# Revit family: WT-Structural Tee
name_source: partatom
category: Structural Framing
revit_build: Autodesk Revit Architecture 2012 (Build: 20110210_1515)
units: mm (PartAtom-declared; Revit-internal decimal feet)

## types (275) — shared parameters
Assembly Code = B10

## per-type parameters (varying)
| type | A | W | bf | d | k | kr | tf | tw |
| WT22X167.5 | 49.2 in² | 168 | 1' - 3 7/8" | 1' - 10" | 0' - 2 5/8" | 0' - 0 7/8" | 0' - 1 3/4" | 0' - 1" |
| WT22X145 | 42.7 in² | 145 | 1' - 3 13/16" | 1' - 9 13/16" | 0' - 2 7/16" | 0' - 0 7/8" | 0' - 1 9/16" | 0' - 0 7/8" |
| WT22X131 | 38.4 in² | 131 | 1' - 3 13/16" | 1' - 9 11/16" | 0' - 2 1/4" | 0' - 0 13/16" | 0' - 1 7/16" | 0' - 0 13/16" |
| WT22X115 | 33.8 in² | 115 | 1' - 3 13/16" | 1' - 9 1/2" | 0' - 2 1/16" | 0' - 0 13/16" | 0' - 1 1/4" | 0' - 0 11/16" |
| WT20X296.5 | 87.2 in² | 296 | 1' - 4 11/16" | 1' - 9 1/2" | 0' - 4 1/2" | 0' - 1 1/4" | 0' - 3 1/4" | 0' - 1 13/16" |
| WT20X251.5 | 73.9 in² | 252 | 1' - 4 3/8" | 1' - 9" | 0' - 4" | 0' - 1 1/4" | 0' - 2 3/4" | 0' - 1 9/16" |
| WT20X215.5 | 63.4 in² | 215 | 1' - 4 3/16" | 1' - 8 5/8" | 0' - 3 5/8" | 0' - 1 1/4" | 0' - 2 3/8" | 0' - 1 5/16" |
| WT20X198.5 | 58.4 in² | 198 | 1' - 4 1/8" | 1' - 8 1/2" | 0' - 3 1/2" | 0' - 1 5/16" | 0' - 2 3/16" | 0' - 1 1/4" |
| WT20X186 | 54.6 in² | 186 | 1' - 4 1/8" | 1' - 8 5/16" | 0' - 3 5/16" | 0' - 1 1/4" | 0' - 2 1/16" | 0' - 1 3/16" |
| WT20X181 | 53.3 in² | 181 | 1' - 4" | 1' - 8 5/16" | 0' - 3 1/4" | 0' - 1 1/4" | 0' - 2" | 0' - 1 1/8" |
| WT20X162 | 47.7 in² | 162 | 1' - 3 7/8" | 1' - 8 1/8" | 0' - 3 1/16" | 0' - 1 1/4" | 0' - 1 13/16" | 0' - 1" |
| WT20X148.5 | 43.7 in² | 148 | 1' - 3 13/16" | 1' - 7 7/8" | 0' - 2 15/16" | 0' - 1 5/16" | 0' - 1 5/8" | 0' - 0 15/16" |
| WT20X138.5 | 40.7 in² | 138 | 1' - 3 13/16" | 1' - 7 13/16" | 0' - 2 7/8" | 0' - 1 5/16" | 0' - 1 9/16" | 0' - 0 13/16" |
| WT20X124.5 | 36.7 in² | 125 | 1' - 3 13/16" | 1' - 7 11/16" | 0' - 2 11/16" | 0' - 1 1/4" | 0' - 1 7/16" | 0' - 0 3/4" |
| WT20X107.5 | 31.7 in² | 108 | 1' - 3 13/16" | 1' - 7 1/2" | 0' - 2 1/2" | 0' - 1 1/4" | 0' - 1 1/4" | 0' - 0 5/8" |
| WT20X99.5 | 29.2 in² | 100 | 1' - 3 13/16" | 1' - 7 5/16" | 0' - 2 5/16" | 0' - 1 1/4" | 0' - 1 1/16" | 0' - 0 5/8" |
| WT20X196 | 57.6 in² | 196 | 1' - 0 3/8" | 1' - 8 13/16" | 0' - 3 13/16" | 0' - 1 5/16" | 0' - 2 1/2" | 0' - 1 7/16" |
| WT20X165.5 | 48.7 in² | 166 | 1' - 0 3/16" | 1' - 8 3/8" | 0' - 3 3/8" | 0' - 1 1/4" | 0' - 2 1/8" | 0' - 1 1/4" |
| WT20X163.5 | 48 in² | 164 | 1' - 0 1/8" | 1' - 8 3/8" | 0' - 3 3/8" | 0' - 1 1/4" | 0' - 2 1/8" | 0' - 1 3/16" |
| WT20X147 | 43.1 in² | 147 | 1' - 0" | 1' - 8 3/16" | 0' - 3 3/16" | 0' - 1 1/4" | 0' - 1 15/16" | 0' - 1 1/16" |
| WT20X139 | 41 in² | 139 | 1' - 0" | 1' - 8 1/8" | 0' - 3 1/16" | 0' - 1 1/4" | 0' - 1 13/16" | 0' - 1" |
| WT20X132 | 38.8 in² | 132 | 0' - 11 7/8" | 1' - 8" | 0' - 3" | 0' - 1 1/4" | 0' - 1 3/4" | 0' - 0 15/16" |
| WT20X117.5 | 34.5 in² | 118 | 0' - 11 7/8" | 1' - 7 13/16" | 0' - 2 7/8" | 0' - 1 5/16" | 0' - 1 9/16" | 0' - 0 13/16" |
| WT20X105.5 | 31 in² | 106 | 0' - 11 13/16" | 1' - 7 11/16" | 0' - 2 11/16" | 0' - 1 1/4" | 0' - 1 7/16" | 0' - 0 3/4" |
| WT20X91.5 | 26.7 in² | 91.5 | 0' - 11 13/16" | 1' - 7 1/2" | 0' - 2 1/2" | 0' - 1 5/16" | 0' - 1 3/16" | 0' - 0 5/8" |
| WT20X83.5 | 24.6 in² | 83.5 | 0' - 11 13/16" | 1' - 7 5/16" | 0' - 2 5/16" | 0' - 1 5/16" | 0' - 1" | 0' - 0 5/8" |
| WT20X74.5 | 21.9 in² | 74.5 | 0' - 11 13/16" | 1' - 7 1/8" | 0' - 2 1/8" | 0' - 1 5/16" | 0' - 0 13/16" | 0' - 0 5/8" |
| WT18X400 | 118 in² | 400 | 1' - 6" | 1' - 9" | 0' - 5 9/16" | 0' - 1 1/4" | 0' - 4 5/16" | 0' - 2 3/8" |
| WT18X326 | 96.1 in² | 325 | 1' - 5 5/8" | 1' - 8 3/16" | 0' - 4 13/16" | 0' - 1 1/4" | 0' - 3 9/16" | 0' - 2" |
| WT18X264.5 | 77.8 in² | 264 | 1' - 5 3/16" | 1' - 7 5/8" | 0' - 4 3/16" | 0' - 1 1/4" | 0' - 2 15/16" | 0' - 1 5/8" |
| WT18X243.5 | 71.7 in² | 244 | 1' - 5 1/8" | 1' - 7 11/16" | 0' - 4" | 0' - 1 5/16" | 0' - 2 11/16" | 0' - 1 1/2" |
| WT18X220.5 | 64.9 in² | 220 | 1' - 5" | 1' - 7 1/8" | 0' - 3 11/16" | 0' - 1 1/4" | 0' - 2 7/16" | 0' - 1 3/8" |
| WT18X197.5 | 58.2 in² | 198 | 1' - 4 13/16" | 1' - 6 7/8" | 0' - 3 7/16" | 0' - 1 1/4" | 0' - 2 3/16" | 0' - 1 1/4" |
| WT18X180.5 | 53 in² | 180 | 1' - 4 11/16" | 1' - 6 11/16" | 0' - 3 1/4" | 0' - 1 1/4" | 0' - 2" | 0' - 1 1/8" |
| WT18X165 | 48.5 in² | 165 | 1' - 4 5/8" | 1' - 6 1/2" | 0' - 3 1/8" | 0' - 1 1/4" | 0' - 1 7/8" | 0' - 1" |
| WT18X151 | 44.4 in² | 151 | 1' - 4 11/16" | 1' - 6 3/8" | 0' - 2 15/16" | 0' - 1 1/4" | 0' - 1 11/16" | 0' - 0 15/16" |
| WT18X141 | 41.5 in² | 141 | 1' - 4 5/8" | 1' - 6 5/16" | 0' - 2 13/16" | 0' - 1 1/4" | 0' - 1 9/16" | 0' - 0 7/8" |
| WT18X131 | 38.5 in² | 131 | 1' - 4 5/8" | 1' - 6 1/8" | 0' - 2 11/16" | 0' - 1 1/4" | 0' - 1 7/16" | 0' - 0 13/16" |
| WT18X123.5 | 36.3 in² | 124 | 1' - 4 1/2" | 1' - 6" | 0' - 2 5/8" | 0' - 1 1/4" | 0' - 1 3/8" | 0' - 0 13/16" |
| WT18X116 | 34.5 in² | 116 | 1' - 0 1/8" | 1' - 6 5/8" | 0' - 2 7/16" | 0' - 0 7/8" | 0' - 1 9/16" | 0' - 0 7/8" |
| WT18X128 | 37.7 in² | 128 | 1' - 0 3/16" | 1' - 6 11/16" | 0' - 2 5/8" | 0' - 0 7/8" | 0' - 1 3/4" | 0' - 0 15/16" |
| WT18X115.5 | 34.1 in² | 116 | 1' - 0 1/8" | 1' - 6 5/8" | 0' - 2 7/16" | 0' - 0 7/8" | 0' - 1 9/16" | 0' - 0 7/8" |
| WT18X105 | 30.9 in² | 105 | 1' - 0 3/16" | 1' - 6 5/16" | 0' - 2 5/16" | 0' - 0 15/16" | 0' - 1 3/8" | 0' - 0 13/16" |
| WT18X97 | 28.5 in² | 97 | 1' - 0 1/8" | 1' - 6 3/16" | 0' - 2 3/16" | 0' - 0 15/16" | 0' - 1 1/4" | 0' - 0 3/4" |
| WT18X91 | 26.8 in² | 91 | 1' - 0 1/8" | 1' - 6 3/16" | 0' - 2 1/8" | 0' - 0 15/16" | 0' - 1 3/16" | 0' - 0 3/4" |
| WT18X85 | 25 in² | 85 | 1' - 0" | 1' - 6 1/8" | 0' - 2" | 0' - 0 7/8" | 0' - 1 1/8" | 0' - 0 11/16" |
| WT18X80 | 23.5 in² | 80 | 1' - 0" | 1' - 6" | 0' - 1 15/16" | 0' - 0 15/16" | 0' - 1" | 0' - 0 5/8" |
| WT18X75 | 22.1 in² | 75 | 1' - 0" | 1' - 5 7/8" | 0' - 1 7/8" | 0' - 0 15/16" | 0' - 0 15/16" | 0' - 0 5/8" |
| WT18X67.5 | 19.9 in² | 67.5 | 1' - 0" | 1' - 5 13/16" | 0' - 1 11/16" | 0' - 0 7/8" | 0' - 0 13/16" | 0' - 0 5/8" |
| WT16.5X193.5 | 57 in² | 194 | 1' - 4 3/16" | 1' - 6" | 0' - 3 3/16" | 0' - 0 15/16" | 0' - 2 1/4" | 0' - 1 1/4" |
| WT16.5X177 | 52.1 in² | 177 | 1' - 4 1/8" | 1' - 5 13/16" | 0' - 2 15/16" | 0' - 0 7/8" | 0' - 2 1/16" | 0' - 1 3/16" |
| WT16.5X159 | 46.8 in² | 159 | 1' - 4" | 1' - 5 5/8" | 0' - 2 3/4" | 0' - 0 7/8" | 0' - 1 7/8" | 0' - 1 1/16" |
| WT16.5X145.5 | 42.8 in² | 146 | 1' - 3 7/8" | 1' - 5 3/8" | 0' - 2 5/8" | 0' - 0 7/8" | 0' - 1 3/4" | 0' - 0 15/16" |
| WT16.5X131.5 | 38.7 in² | 132 | 1' - 3 13/16" | 1' - 5 5/16" | 0' - 2 7/16" | 0' - 0 7/8" | 0' - 1 9/16" | 0' - 0 7/8" |
| WT16.5X120.5 | 35.5 in² | 120 | 1' - 3 7/8" | 1' - 5 1/8" | 0' - 2 1/4" | 0' - 0 7/8" | 0' - 1 3/8" | 0' - 0 13/16" |
| WT16.5X110.5 | 32.6 in² | 110 | 1' - 3 13/16" | 1' - 5" | 0' - 2 1/8" | 0' - 0 7/8" | 0' - 1 1/4" | 0' - 0 3/4" |
| WT16.5X100.5 | 29.6 in² | 100 | 1' - 3 11/16" | 1' - 4 13/16" | 0' - 2" | 0' - 0 7/8" | 0' - 1 1/8" | 0' - 0 11/16" |
| WT16.5X84.5 | 24.8 in² | 84.5 | 0' - 11 1/2" | 1' - 4 7/8" | 0' - 2 1/8" | 0' - 0 7/8" | 0' - 1 1/4" | 0' - 0 11/16" |
| WT16.5X76 | 22.4 in² | 76 | 0' - 11 5/8" | 1' - 4 11/16" | 0' - 1 15/16" | 0' - 0 7/8" | 0' - 1 1/16" | 0' - 0 5/8" |
| WT16.5X70.5 | 20.8 in² | 70.5 | 0' - 11 1/2" | 1' - 4 11/16" | 0' - 1 13/16" | 0' - 0 7/8" | 0' - 0 15/16" | 0' - 0 5/8" |
| WT16.5X65 | 19.2 in² | 65 | 0' - 11 1/2" | 1' - 4 1/2" | 0' - 1 3/4" | 0' - 0 7/8" | 0' - 0 7/8" | 0' - 0 9/16" |
| WT16.5X59 | 17.3 in² | 59 | 0' - 11 1/2" | 1' - 4 3/8" | 0' - 1 5/8" | 0' - 0 7/8" | 0' - 0 3/4" | 0' - 0 9/16" |
| WT15X195.5 | 57.6 in² | 196 | 1' - 3 5/8" | 1' - 4 5/8" | 0' - 3 3/8" | 0' - 0 15/16" | 0' - 2 7/16" | 0' - 1 3/8" |
| WT15X178.5 | 52.5 in² | 178 | 1' - 3 1/2" | 1' - 4 3/8" | 0' - 3 1/8" | 0' - 0 7/8" | 0' - 2 1/4" | 0' - 1 1/4" |
| WT15X163 | 47.9 in² | 163 | 1' - 3 3/8" | 1' - 4 3/16" | 0' - 2 15/16" | 0' - 0 7/8" | 0' - 2 1/16" | 0' - 1 1/8" |
| WT15X146 | 42.9 in² | 146 | 1' - 3 5/16" | 1' - 4" | 0' - 2 3/4" | 0' - 0 7/8" | 0' - 1 7/8" | 0' - 1" |
| WT15X130.5 | 38.4 in² | 130 | 1' - 3 3/16" | 1' - 3 13/16" | 0' - 2 9/16" | 0' - 0 15/16" | 0' - 1 5/8" | 0' - 0 15/16" |
| WT15X117.5 | 34.6 in² | 118 | 1' - 3 1/8" | 1' - 3 11/16" | 0' - 2 3/8" | 0' - 0 7/8" | 0' - 1 1/2" | 0' - 0 13/16" |
| WT15X105.5 | 31.1 in² | 106 | 1' - 3 1/8" | 1' - 3 1/2" | 0' - 2 1/4" | 0' - 0 15/16" | 0' - 1 5/16" | 0' - 0 3/4" |
| WT15X95.5 | 28.1 in² | 95.5 | 1' - 3" | 1' - 3 5/16" | 0' - 2 1/16" | 0' - 0 7/8" | 0' - 1 3/16" | 0' - 0 11/16" |
| WT15X86.5 | 25.5 in² | 86.5 | 1' - 3" | 1' - 3 3/16" | 0' - 2" | 0' - 0 15/16" | 0' - 1 1/16" | 0' - 0 5/8" |
| WT15X74 | 21.7 in² | 74 | 0' - 10 1/2" | 1' - 3 5/16" | 0' - 2 1/16" | 0' - 0 7/8" | 0' - 1 3/16" | 0' - 0 5/8" |
| WT15X66 | 19.4 in² | 66 | 0' - 10 1/2" | 1' - 3 3/16" | 0' - 1 7/8" | 0' - 0 7/8" | 0' - 1" | 0' - 0 5/8" |
| WT15X62 | 18.2 in² | 62 | 0' - 10 1/2" | 1' - 3 1/8" | 0' - 1 13/16" | 0' - 0 7/8" | 0' - 0 15/16" | 0' - 0 9/16" |
| WT15X58 | 17.1 in² | 58 | 0' - 10 1/2" | 1' - 3" | 0' - 1 3/4" | 0' - 0 7/8" | 0' - 0 7/8" | 0' - 0 9/16" |
| WT15X54 | 15.9 in² | 54 | 0' - 10 1/2" | 1' - 2 7/8" | 0' - 1 11/16" | 0' - 0 15/16" | 0' - 0 3/4" | 0' - 0 9/16" |
| WT15X49.5 | 14.5 in² | 49.5 | 0' - 10 1/2" | 1' - 2 13/16" | 0' - 1 9/16" | 0' - 0 7/8" | 0' - 0 11/16" | 0' - 0 1/2" |
| WT15X45 | 13.2 in² | 45 | 0' - 10 3/8" | 1' - 2 13/16" | 0' - 1 1/2" | 0' - 0 7/8" | 0' - 0 5/8" | 0' - 0 1/2" |
| WT13.5X269.5 | 79.3 in² | 270 | 1' - 3 5/16" | 1' - 4 5/16" | 0' - 4 7/16" | 0' - 0 7/8" | 0' - 3 9/16" | 0' - 2" |
| WT13.5X184 | 54.2 in² | 184 | 1' - 2 11/16" | 1' - 3 3/16" | 0' - 3 3/8" | 0' - 0 7/8" | 0' - 2 1/2" | 0' - 1 3/8" |
| WT13.5X168 | 49.5 in² | 168 | 1' - 2 5/8" | 1' - 3" | 0' - 3 3/16" | 0' - 0 15/16" | 0' - 2 1/4" | 0' - 1 1/4" |
| WT13.5X153.5 | 45.2 in² | 154 | 1' - 2 3/8" | 1' - 2 13/16" | 0' - 3" | 0' - 0 15/16" | 0' - 2 1/16" | 0' - 1 3/16" |
| WT13.5X140.5 | 41.4 in² | 140 | 1' - 2 3/8" | 1' - 2 5/8" | 0' - 2 13/16" | 0' - 0 7/8" | 0' - 1 15/16" | 0' - 1 1/16" |
| WT13.5X129 | 38 in² | 129 | 1' - 2 5/16" | 1' - 2 1/2" | 0' - 2 11/16" | 0' - 0 15/16" | 0' - 1 3/4" | 0' - 1" |
| WT13.5X117.5 | 34.7 in² | 118 | 1' - 2 3/16" | 1' - 2 5/16" | 0' - 2 1/2" | 0' - 0 7/8" | 0' - 1 5/8" | 0' - 0 15/16" |
| WT13.5X108.5 | 32 in² | 108 | 1' - 2 1/8" | 1' - 2 3/16" | 0' - 2 3/8" | 0' - 0 7/8" | 0' - 1 1/2" | 0' - 0 13/16" |
| WT13.5X97 | 28.6 in² | 97 | 1' - 2" | 1' - 2 1/8" | 0' - 2 1/4" | 0' - 0 15/16" | 0' - 1 5/16" | 0' - 0 3/4" |
| WT13.5X89 | 26.2 in² | 89 | 1' - 2 1/8" | 1' - 1 7/8" | 0' - 2 1/16" | 0' - 0 7/8" | 0' - 1 3/16" | 0' - 0 3/4" |
| WT13.5X80.5 | 23.8 in² | 80.5 | 1' - 2" | 1' - 1 13/16" | 0' - 2" | 0' - 0 15/16" | 0' - 1 1/16" | 0' - 0 11/16" |
| WT13.5X73 | 21.6 in² | 73 | 1' - 2" | 1' - 1 11/16" | 0' - 1 7/8" | 0' - 0 7/8" | 0' - 1" | 0' - 0 5/8" |
| WT13.5X64.5 | 18.9 in² | 64.5 | 0' - 10" | 1' - 1 13/16" | 0' - 2" | 0' - 0 7/8" | 0' - 1 1/8" | 0' - 0 5/8" |
| WT13.5X57 | 16.8 in² | 57 | 0' - 10 1/8" | 1' - 1 5/8" | 0' - 1 13/16" | 0' - 0 7/8" | 0' - 0 15/16" | 0' - 0 9/16" |
| WT13.5X51 | 15 in² | 51 | 0' - 10" | 1' - 1 1/2" | 0' - 1 3/4" | 0' - 0 15/16" | 0' - 0 13/16" | 0' - 0 1/2" |
| WT13.5X47 | 13.8 in² | 47 | 0' - 10" | 1' - 1 1/2" | 0' - 1 5/8" | 0' - 0 7/8" | 0' - 0 3/4" | 0' - 0 1/2" |
| WT13.5X42 | 12.4 in² | 42 | 0' - 10" | 1' - 1 3/8" | 0' - 1 9/16" | 0' - 0 15/16" | 0' - 0 5/8" | 0' - 0 7/16" |
| WT12X185 | 54.4 in² | 185 | 1' - 1 11/16" | 1' - 2" | 0' - 3 5/8" | 0' - 0 7/8" | 0' - 2 3/4" | 0' - 1 1/2" |
| WT12X167.5 | 49.2 in² | 168 | 1' - 1 1/2" | 1' - 1 13/16" | 0' - 3 3/8" | 0' - 0 7/8" | 0' - 2 1/2" | 0' - 1 3/8" |
| WT12X153 | 44.9 in² | 153 | 1' - 1 3/8" | 1' - 1 5/8" | 0' - 3 3/16" | 0' - 0 15/16" | 0' - 2 1/4" | 0' - 1 1/4" |
| WT12X139.5 | 41 in² | 140 | 1' - 1 5/16" | 1' - 1 3/8" | 0' - 3" | 0' - 0 15/16" | 0' - 2 1/16" | 0' - 1 3/16" |
| WT12X125 | 36.8 in² | 125 | 1' - 1 3/16" | 1' - 1 3/16" | 0' - 2 13/16" | 0' - 0 15/16" | 0' - 1 7/8" | 0' - 1 1/16" |
| WT12X114.5 | 33.6 in² | 114 | 1' - 1 1/8" | 1' - 1" | 0' - 2 5/8" | 0' - 0 7/8" | 0' - 1 3/4" | 0' - 0 15/16" |
| WT12X103.5 | 30.4 in² | 103 | 1' - 1" | 1' - 0 7/8" | 0' - 2 1/2" | 0' - 0 15/16" | 0' - 1 9/16" | 0' - 0 7/8" |
| WT12X96 | 28.1 in² | 96 | 1' - 1" | 1' - 0 11/16" | 0' - 2 3/8" | 0' - 0 15/16" | 0' - 1 7/16" | 0' - 0 13/16" |
| WT12X88 | 25.8 in² | 88 | 1' - 0 7/8" | 1' - 0 5/8" | 0' - 2 1/4" | 0' - 0 15/16" | 0' - 1 5/16" | 0' - 0 3/4" |
| WT12X81 | 23.9 in² | 81 | 1' - 1" | 1' - 0 1/2" | 0' - 2 1/8" | 0' - 0 7/8" | 0' - 1 1/4" | 0' - 0 11/16" |
| WT12X73 | 21.5 in² | 73 | 1' - 0 7/8" | 1' - 0 3/8" | 0' - 2" | 0' - 0 15/16" | 0' - 1 1/16" | 0' - 0 5/8" |
| WT12X65.5 | 19.3 in² | 65.5 | 1' - 0 7/8" | 1' - 0 3/16" | 0' - 1 7/8" | 0' - 0 15/16" | 0' - 0 15/16" | 0' - 0 5/8" |
| WT12X58.5 | 17.2 in² | 58.5 | 1' - 0 13/16" | 1' - 0 1/8" | 0' - 1 3/4" | 0' - 0 7/8" | 0' - 0 7/8" | 0' - 0 9/16" |
| WT12X52 | 15.3 in² | 52 | 1' - 0 13/16" | 1' - 0" | 0' - 1 5/8" | 0' - 0 7/8" | 0' - 0 3/4" | 0' - 0 1/2" |
| WT12X51.5 | 15.1 in² | 51.5 | 0' - 9" | 1' - 0 5/16" | 0' - 1 7/8" | 0' - 0 7/8" | 0' - 1" | 0' - 0 9/16" |
| WT12X47 | 13.8 in² | 47 | 0' - 9 1/16" | 1' - 0 3/16" | 0' - 1 3/4" | 0' - 0 7/8" | 0' - 0 7/8" | 0' - 0 1/2" |
| WT12X42 | 12.4 in² | 42 | 0' - 9" | 1' - 0 1/8" | 0' - 1 11/16" | 0' - 0 15/16" | 0' - 0 3/4" | 0' - 0 1/2" |
| WT12X38 | 11.2 in² | 38 | 0' - 9" | 1' - 0" | 0' - 1 9/16" | 0' - 0 7/8" | 0' - 0 11/16" | 0' - 0 7/16" |
| WT12X34 | 10 in² | 34 | 0' - 9" | 0' - 11 7/8" | 0' - 1 1/2" | 0' - 0 15/16" | 0' - 0 9/16" | 0' - 0 7/16" |
| WT12X31 | 9.11 in² | 31 | 0' - 7 1/16" | 0' - 11 7/8" | 0' - 1 1/2" | 0' - 0 15/16" | 0' - 0 9/16" | 0' - 0 7/16" |
| WT12X27.5 | 8.1 in² | 27.5 | 0' - 7" | 0' - 11 13/16" | 0' - 1 7/16" | 0' - 0 15/16" | 0' - 0 1/2" | 0' - 0 3/8" |
| WT10.5X100.5 | 29.6 in² | 100 | 1' - 0 5/8" | 0' - 11 1/2" | 0' - 2 1/2" | 0' - 0 7/8" | 0' - 1 5/8" | 0' - 0 15/16" |
| WT10.5X91 | 26.8 in² | 91 | 1' - 0 1/2" | 0' - 11 3/8" | 0' - 2 3/8" | 0' - 0 7/8" | 0' - 1 1/2" | 0' - 0 13/16" |
| WT10.5X83 | 24.4 in² | 83 | 1' - 0 3/8" | 0' - 11 3/16" | 0' - 2 1/4" | 0' - 0 7/8" | 0' - 1 3/8" | 0' - 0 3/4" |
| WT10.5X73.5 | 21.6 in² | 73.5 | 1' - 0 1/2" | 0' - 11" | 0' - 2" | 0' - 0 7/8" | 0' - 1 1/8" | 0' - 0 3/4" |
| WT10.5X66 | 19.4 in² | 66 | 1' - 0 3/8" | 0' - 10 7/8" | 0' - 1 15/16" | 0' - 0 7/8" | 0' - 1 1/16" | 0' - 0 5/8" |
| WT10.5X61 | 17.9 in² | 61 | 1' - 0 3/8" | 0' - 10 13/16" | 0' - 1 13/16" | 0' - 0 7/8" | 0' - 0 15/16" | 0' - 0 5/8" |
| WT10.5X55.5 | 16.3 in² | 55.5 | 1' - 0 5/16" | 0' - 10 13/16" | 0' - 1 3/4" | 0' - 0 7/8" | 0' - 0 7/8" | 0' - 0 9/16" |
| WT10.5X50.5 | 14.9 in² | 50.5 | 1' - 0 5/16" | 0' - 10 11/16" | 0' - 1 11/16" | 0' - 0 7/8" | 0' - 0 13/16" | 0' - 0 1/2" |
| WT10.5X46.5 | 13.7 in² | 46.5 | 0' - 8 7/16" | 0' - 10 13/16" | 0' - 1 5/8" | 0' - 0 11/16" | 0' - 0 15/16" | 0' - 0 9/16" |
| WT10.5X41.5 | 12.2 in² | 41.5 | 0' - 8 3/8" | 0' - 10 11/16" | 0' - 1 1/2" | 0' - 0 11/16" | 0' - 0 13/16" | 0' - 0 1/2" |
| WT10.5X36.5 | 10.7 in² | 36.5 | 0' - 8 5/16" | 0' - 10 5/8" | 0' - 1 7/16" | 0' - 0 11/16" | 0' - 0 3/4" | 0' - 0 7/16" |
| WT10.5X34 | 10 in² | 34 | 0' - 8 1/4" | 0' - 10 5/8" | 0' - 1 3/8" | 0' - 0 11/16" | 0' - 0 11/16" | 0' - 0 7/16" |
| WT10.5X31 | 9.13 in² | 31 | 0' - 8 1/4" | 0' - 10 1/2" | 0' - 1 5/16" | 0' - 0 11/16" | 0' - 0 5/8" | 0' - 0 3/8" |
| WT10.5X27.5 | 8.1 in² | 27.5 | 0' - 8 1/4" | 0' - 10 3/8" | 0' - 1 3/16" | 0' - 0 11/16" | 0' - 0 1/2" | 0' - 0 3/8" |
| WT10.5X24 | 7.07 in² | 24 | 0' - 8 1/8" | 0' - 10 5/16" | 0' - 1 1/8" | 0' - 0 11/16" | 0' - 0 7/16" | 0' - 0 3/8" |
| WT10.5X28.5 | 8.37 in² | 28.5 | 0' - 6 9/16" | 0' - 10 1/2" | 0' - 1 5/16" | 0' - 0 11/16" | 0' - 0 5/8" | 0' - 0 3/8" |
| WT10.5X25 | 7.36 in² | 25 | 0' - 6 1/2" | 0' - 10 3/8" | 0' - 1 1/4" | 0' - 0 11/16" | 0' - 0 9/16" | 0' - 0 3/8" |
| WT10.5X22 | 6.49 in² | 22 | 0' - 6 1/2" | 0' - 10 5/16" | 0' - 1 1/8" | 0' - 0 11/16" | 0' - 0 7/16" | 0' - 0 3/8" |
| WT9X155.5 | 45.8 in² | 156 | 1' - 0" | 0' - 11 3/16" | 0' - 3 7/16" | 0' - 0 11/16" | 0' - 2 3/4" | 0' - 1 1/2" |
| WT9X141.5 | 41.6 in² | 142 | 0' - 11 7/8" | 0' - 10 7/8" | 0' - 3 3/16" | 0' - 0 11/16" | 0' - 2 1/2" | 0' - 1 3/8" |
| WT9X129 | 37.9 in² | 129 | 0' - 11 13/16" | 0' - 10 11/16" | 0' - 3" | 0' - 0 11/16" | 0' - 2 5/16" | 0' - 1 1/4" |
| WT9X117 | 34.4 in² | 117 | 0' - 11 11/16" | 0' - 10 1/2" | 0' - 2 3/4" | 0' - 0 5/8" | 0' - 2 1/8" | 0' - 1 3/16" |
| WT9X105.5 | 31.1 in² | 106 | 0' - 11 5/8" | 0' - 10 5/16" | 0' - 2 9/16" | 0' - 0 5/8" | 0' - 1 15/16" | 0' - 1 1/16" |
| WT9X96 | 28.2 in² | 97 | 0' - 11 1/2" | 0' - 10 3/16" | 0' - 2 7/16" | 0' - 0 11/16" | 0' - 1 3/4" | 0' - 0 15/16" |
| WT9X87.5 | 25.7 in² | 87.5 | 0' - 11 3/8" | 0' - 10" | 0' - 2 7/16" | 0' - 0 7/8" | 0' - 1 9/16" | 0' - 0 7/8" |
| WT9X79 | 23.2 in² | 79 | 0' - 11 5/16" | 0' - 9 7/8" | 0' - 2 3/8" | 0' - 0 15/16" | 0' - 1 7/16" | 0' - 0 13/16" |
| WT9X71.5 | 21 in² | 71.5 | 0' - 11 3/16" | 0' - 9 3/4" | 0' - 2 3/16" | 0' - 0 7/8" | 0' - 1 5/16" | 0' - 0 3/4" |
| WT9X65 | 19.1 in² | 65 | 0' - 11 3/16" | 0' - 9 5/8" | 0' - 2 1/16" | 0' - 0 7/8" | 0' - 1 3/16" | 0' - 0 11/16" |
| WT9X59.5 | 17.5 in² | 59.5 | 0' - 11 5/16" | 0' - 9 1/2" | 0' - 1 15/16" | 0' - 0 7/8" | 0' - 1 1/16" | 0' - 0 5/8" |
| WT9X53 | 15.6 in² | 53 | 0' - 11 3/16" | 0' - 9 3/8" | 0' - 1 13/16" | 0' - 0 7/8" | 0' - 0 15/16" | 0' - 0 9/16" |
| WT9X48.5 | 14.3 in² | 48.5 | 0' - 11 1/8" | 0' - 9 5/16" | 0' - 1 3/4" | 0' - 0 7/8" | 0' - 0 7/8" | 0' - 0 9/16" |
| WT9X43 | 12.7 in² | 43 | 0' - 11 1/8" | 0' - 9 3/16" | 0' - 1 5/8" | 0' - 0 7/8" | 0' - 0 3/4" | 0' - 0 1/2" |
| WT9X38 | 11.2 in² | 38 | 0' - 11" | 0' - 9 1/8" | 0' - 1 9/16" | 0' - 0 7/8" | 0' - 0 11/16" | 0' - 0 7/16" |
| WT9X35.5 | 10.4 in² | 35.5 | 0' - 7 5/8" | 0' - 9 1/4" | 0' - 1 1/2" | 0' - 0 11/16" | 0' - 0 13/16" | 0' - 0 1/2" |
| WT9X32.5 | 9.55 in² | 32.5 | 0' - 7 9/16" | 0' - 9 3/16" | 0' - 1 7/16" | 0' - 0 11/16" | 0' - 0 3/4" | 0' - 0 7/16" |
| WT9X30 | 8.82 in² | 30 | 0' - 7 9/16" | 0' - 9 1/8" | 0' - 1 3/8" | 0' - 0 11/16" | 0' - 0 11/16" | 0' - 0 7/16" |
| WT9X27.5 | 8.1 in² | 27.5 | 0' - 7 1/2" | 0' - 9 1/16" | 0' - 1 5/16" | 0' - 0 11/16" | 0' - 0 5/8" | 0' - 0 3/8" |
| WT9X25 | 7.33 in² | 25 | 0' - 7 1/2" | 0' - 9" | 0' - 1 1/4" | 0' - 0 11/16" | 0' - 0 9/16" | 0' - 0 3/8" |
| WT9X23 | 6.77 in² | 23 | 0' - 6 1/16" | 0' - 9" | 0' - 1 1/4" | 0' - 0 5/8" | 0' - 0 5/8" | 0' - 0 3/8" |
| WT9X20 | 5.88 in² | 20 | 0' - 6" | 0' - 8 15/16" | 0' - 1 3/16" | 0' - 0 11/16" | 0' - 0 1/2" | 0' - 0 5/16" |
| WT9X17.5 | 5.15 in² | 17.5 | 0' - 6" | 0' - 8 7/8" | 0' - 1 1/8" | 0' - 0 11/16" | 0' - 0 7/16" | 0' - 0 5/16" |
| WT8X50 | 14.7 in² | 50 | 0' - 10 3/8" | 0' - 8 1/2" | 0' - 1 7/8" | 0' - 0 7/8" | 0' - 1" | 0' - 0 9/16" |
| WT8X44.5 | 13.1 in² | 44.5 | 0' - 10 3/8" | 0' - 8 3/8" | 0' - 1 3/4" | 0' - 0 7/8" | 0' - 0 7/8" | 0' - 0 1/2" |
| WT8X38.5 | 11.3 in² | 38.5 | 0' - 10 5/16" | 0' - 8 1/4" | 0' - 1 5/8" | 0' - 0 7/8" | 0' - 0 3/4" | 0' - 0 7/16" |
| WT8X33.5 | 9.84 in² | 33.5 | 0' - 10 3/16" | 0' - 8 3/16" | 0' - 1 9/16" | 0' - 0 7/8" | 0' - 0 11/16" | 0' - 0 3/8" |
| WT8X28.5 | 8.39 in² | 28.5 | 0' - 7 1/8" | 0' - 8 1/4" | 0' - 1 3/8" | 0' - 0 11/16" | 0' - 0 11/16" | 0' - 0 7/16" |
| WT8X25 | 7.37 in² | 25 | 0' - 7 1/16" | 0' - 8 1/8" | 0' - 1 5/16" | 0' - 0 11/16" | 0' - 0 5/8" | 0' - 0 3/8" |
| WT8X22.5 | 6.63 in² | 22.5 | 0' - 7 1/16" | 0' - 8 1/16" | 0' - 1 1/4" | 0' - 0 11/16" | 0' - 0 9/16" | 0' - 0 3/8" |
| WT8X20 | 5.89 in² | 20 | 0' - 7" | 0' - 8" | 0' - 1 3/16" | 0' - 0 11/16" | 0' - 0 1/2" | 0' - 0 5/16" |
| WT8X18 | 5.29 in² | 18 | 0' - 7" | 0' - 7 15/16" | 0' - 1 1/8" | 0' - 0 11/16" | 0' - 0 7/16" | 0' - 0 5/16" |
| WT8X15.5 | 4.56 in² | 15.5 | 0' - 5 1/2" | 0' - 7 15/16" | 0' - 1 1/8" | 0' - 0 11/16" | 0' - 0 7/16" | 0' - 0 1/4" |
| WT8X13 | 3.84 in² | 13 | 0' - 5 1/2" | 0' - 7 7/8" | 0' - 1 1/16" | 0' - 0 11/16" | 0' - 0 3/8" | 0' - 0 1/4" |
| WT7X404 - Obsolete | 119 in² | 404 | 1' - 6 5/8" | 0' - 11 3/8" | 0' - 6 7/16" | 0' - 1 5/16" | 0' - 5 1/8" | 0' - 3 3/4" |
| WT7X365 | 107 in² | 365 | 1' - 5 7/8" | 0' - 11 3/16" | 0' - 6 3/16" | 0' - 1 1/4" | 0' - 4 15/16" | 0' - 3 1/16" |
| WT7X332.5 | 97.8 in² | 332 | 1' - 5 11/16" | 0' - 10 13/16" | 0' - 5 13/16" | 0' - 1 5/16" | 0' - 4 1/2" | 0' - 2 13/16" |
| WT7X302.5 | 88.9 in² | 302 | 1' - 5 3/8" | 0' - 10 1/2" | 0' - 5 7/16" | 0' - 1 1/4" | 0' - 4 3/16" | 0' - 2 5/8" |
| WT7X275 | 80.9 in² | 275 | 1' - 5 3/16" | 0' - 10 1/8" | 0' - 5 1/8" | 0' - 1 5/16" | 0' - 3 13/16" | 0' - 2 3/8" |
| WT7X250 | 73.5 in² | 250 | 1' - 5" | 0' - 9 13/16" | 0' - 4 13/16" | 0' - 1 5/16" | 0' - 3 1/2" | 0' - 2 3/16" |
| WT7X227.5 | 66.9 in² | 228 | 1' - 4 13/16" | 0' - 9 1/2" | 0' - 4 1/2" | 0' - 1 5/16" | 0' - 3 3/16" | 0' - 2" |
| WT7X213 | 62.6 in² | 213 | 1' - 4 11/16" | 0' - 9 5/16" | 0' - 4 5/16" | 0' - 1 1/4" | 0' - 3 1/16" | 0' - 1 7/8" |
| WT7X199 | 58.5 in² | 199 | 1' - 4 5/8" | 0' - 9 1/8" | 0' - 4 1/8" | 0' - 1 1/4" | 0' - 2 7/8" | 0' - 1 3/4" |
| WT7X185 | 54.4 in² | 185 | 1' - 4 1/2" | 0' - 8 15/16" | 0' - 3 15/16" | 0' - 1 1/4" | 0' - 2 11/16" | 0' - 1 11/16" |
| WT7X171 | 50.3 in² | 171 | 1' - 4 3/8" | 0' - 8 3/4" | 0' - 3 3/4" | 0' - 1 1/4" | 0' - 2 1/2" | 0' - 1 9/16" |
| WT7X155.5 | 45.7 in² | 156 | 1' - 4 3/16" | 0' - 8 9/16" | 0' - 3 9/16" | 0' - 1 5/16" | 0' - 2 1/4" | 0' - 1 7/16" |
| WT7X141.5 | 41.6 in² | 142 | 1' - 4 1/8" | 0' - 8 3/8" | 0' - 3 3/8" | 0' - 1 5/16" | 0' - 2 1/16" | 0' - 1 5/16" |
| WT7X128.5 | 37.8 in² | 128 | 1' - 4" | 0' - 8 3/16" | 0' - 3 3/16" | 0' - 1 5/16" | 0' - 1 7/8" | 0' - 1 3/16" |
| WT7X116.5 | 34.2 in² | 116 | 1' - 3 7/8" | 0' - 8" | 0' - 3" | 0' - 1 1/4" | 0' - 1 3/4" | 0' - 1 1/16" |
| WT7X105.5 | 31 in² | 106 | 1' - 3 13/16" | 0' - 7 7/8" | 0' - 2 7/8" | 0' - 1 5/16" | 0' - 1 9/16" | 0' - 1" |
| WT7X96.5 | 28.4 in² | 96.5 | 1' - 3 11/16" | 0' - 7 3/4" | 0' - 2 3/4" | 0' - 1 5/16" | 0' - 1 7/16" | 0' - 0 7/8" |
| WT7X88 | 25.9 in² | 88 | 1' - 3 11/16" | 0' - 7 5/8" | 0' - 2 5/8" | 0' - 1 5/16" | 0' - 1 5/16" | 0' - 0 13/16" |
| WT7X79.5 | 23.4 in² | 79.5 | 1' - 3 5/8" | 0' - 7 1/2" | 0' - 2 1/2" | 0' - 1 5/16" | 0' - 1 3/16" | 0' - 0 3/4" |
| WT7X72.5 | 21.3 in² | 72.5 | 1' - 3 1/2" | 0' - 7 3/8" | 0' - 2 3/8" | 0' - 1 5/16" | 0' - 1 1/16" | 0' - 0 11/16" |
| WT7X66 | 19.4 in² | 66 | 1' - 2 11/16" | 0' - 7 5/16" | 0' - 2 5/16" | 0' - 1 5/16" | 0' - 1" | 0' - 0 5/8" |
| WT7X60 | 17.7 in² | 60 | 1' - 2 11/16" | 0' - 7 1/4" | 0' - 2 1/4" | 0' - 1 5/16" | 0' - 0 15/16" | 0' - 0 9/16" |
| WT7X54.5 | 16 in² | 54.5 | 1' - 2 5/8" | 0' - 7 3/16" | 0' - 2 3/16" | 0' - 1 5/16" | 0' - 0 7/8" | 0' - 0 1/2" |
| WT7X49.5 | 14.6 in² | 49.5 | 1' - 2 5/8" | 0' - 7 1/16" | 0' - 2 1/16" | 0' - 1 5/16" | 0' - 0 3/4" | 0' - 0 1/2" |
| WT7X45 | 13.2 in² | 45 | 1' - 2 1/2" | 0' - 7" | 0' - 2" | 0' - 1 5/16" | 0' - 0 11/16" | 0' - 0 7/16" |
| WT7X41 | 12 in² | 41 | 0' - 10 1/8" | 0' - 7 3/16" | 0' - 1 11/16" | 0' - 0 13/16" | 0' - 0 7/8" | 0' - 0 1/2" |
| WT7X37 | 10.9 in² | 37 | 0' - 10 1/8" | 0' - 7 1/16" | 0' - 1 5/8" | 0' - 0 13/16" | 0' - 0 13/16" | 0' - 0 7/16" |
| WT7X34 | 10 in² | 34 | 0' - 10" | 0' - 7" | 0' - 1 9/16" | 0' - 0 13/16" | 0' - 0 3/4" | 0' - 0 7/16" |
| WT7X30.5 | 8.96 in² | 30.5 | 0' - 10" | 0' - 6 15/16" | 0' - 1 1/2" | 0' - 0 7/8" | 0' - 0 5/8" | 0' - 0 3/8" |
| WT7X26.5 | 7.8 in² | 26.5 | 0' - 8 1/16" | 0' - 6 15/16" | 0' - 1 1/2" | 0' - 0 13/16" | 0' - 0 11/16" | 0' - 0 3/8" |
| WT7X24 | 7.07 in² | 24 | 0' - 8" | 0' - 6 7/8" | 0' - 1 7/16" | 0' - 0 13/16" | 0' - 0 5/8" | 0' - 0 5/16" |
| WT7X21.5 | 6.31 in² | 21.5 | 0' - 8" | 0' - 6 13/16" | 0' - 1 3/8" | 0' - 0 7/8" | 0' - 0 1/2" | 0' - 0 5/16" |
| WT7X19 | 5.58 in² | 19 | 0' - 6 3/4" | 0' - 7 1/16" | 0' - 1 1/4" | 0' - 0 3/4" | 0' - 0 1/2" | 0' - 0 5/16" |
| WT7X17 | 5 in² | 17 | 0' - 6 3/4" | 0' - 7" | 0' - 1 3/16" | 0' - 0 3/4" | 0' - 0 7/16" | 0' - 0 5/16" |
| WT7X15 | 4.42 in² | 15 | 0' - 6 3/4" | 0' - 6 15/16" | 0' - 1 1/8" | 0' - 0 3/4" | 0' - 0 3/8" | 0' - 0 1/4" |
| WT7X13 | 3.85 in² | 13 | 0' - 5" | 0' - 6 15/16" | 0' - 1 1/8" | 0' - 0 11/16" | 0' - 0 7/16" | 0' - 0 1/4" |
| WT7X11 | 3.25 in² | 11 | 0' - 5" | 0' - 6 7/8" | 0' - 1 1/16" | 0' - 0 3/4" | 0' - 0 5/16" | 0' - 0 1/4" |
| WT6X168 | 49.4 in² | 168 | 1' - 1 3/8" | 0' - 8 7/16" | 0' - 3 7/8" | 0' - 0 15/16" | 0' - 2 15/16" | 0' - 1 3/4" |
| WT6X152.5 | 44.8 in² | 152 | 1' - 1 3/16" | 0' - 8 3/16" | 0' - 3 5/8" | 0' - 0 15/16" | 0' - 2 11/16" | 0' - 1 5/8" |
| WT6X139.5 | 41 in² | 140 | 1' - 1 1/8" | 0' - 7 15/16" | 0' - 3 3/8" | 0' - 0 7/8" | 0' - 2 1/2" | 0' - 1 1/2" |
| WT6X126 | 37 in² | 126 | 1' - 1" | 0' - 7 11/16" | 0' - 3 1/8" | 0' - 0 7/8" | 0' - 2 1/4" | 0' - 1 3/8" |
| WT6X115 | 33.9 in² | 115 | 1' - 0 7/8" | 0' - 7 1/2" | 0' - 2 15/16" | 0' - 0 7/8" | 0' - 2 1/16" | 0' - 1 5/16" |
| WT6X105 | 30.9 in² | 105 | 1' - 0 13/16" | 0' - 7 3/8" | 0' - 2 13/16" | 0' - 0 15/16" | 0' - 1 7/8" | 0' - 1 3/16" |
| WT6X95 | 27.9 in² | 95 | 1' - 0 11/16" | 0' - 7 3/16" | 0' - 2 5/8" | 0' - 0 7/8" | 0' - 1 3/4" | 0' - 1 1/16" |
| WT6X85 | 25 in² | 85 | 1' - 0 5/8" | 0' - 7" | 0' - 2 7/16" | 0' - 0 7/8" | 0' - 1 9/16" | 0' - 0 15/16" |
| WT6X76 | 22.4 in² | 76 | 1' - 0 1/2" | 0' - 6 7/8" | 0' - 2 5/16" | 0' - 0 15/16" | 0' - 1 3/8" | 0' - 0 7/8" |
| WT6X68 | 20 in² | 68 | 1' - 0 3/8" | 0' - 6 11/16" | 0' - 2 1/8" | 0' - 0 7/8" | 0' - 1 1/4" | 0' - 0 13/16" |
| WT6X60 | 17.6 in² | 60 | 1' - 0 5/16" | 0' - 6 9/16" | 0' - 2" | 0' - 0 7/8" | 0' - 1 1/8" | 0' - 0 11/16" |
| WT6X53 | 15.6 in² | 53 | 1' - 0 3/16" | 0' - 6 7/16" | 0' - 1 7/8" | 0' - 0 7/8" | 0' - 1" | 0' - 0 5/8" |
| WT6X48 | 14.1 in² | 48 | 1' - 0 3/16" | 0' - 6 3/8" | 0' - 1 13/16" | 0' - 0 15/16" | 0' - 0 7/8" | 0' - 0 9/16" |
| WT6X43.5 | 12.8 in² | 43.5 | 1' - 0 1/8" | 0' - 6 1/4" | 0' - 1 11/16" | 0' - 0 7/8" | 0' - 0 13/16" | 0' - 0 1/2" |
| WT6X39.5 | 11.6 in² | 39.5 | 1' - 0 1/8" | 0' - 6 3/16" | 0' - 1 5/8" | 0' - 0 7/8" | 0' - 0 3/4" | 0' - 0 1/2" |
| WT6X36 | 10.6 in² | 36 | 1' - 0" | 0' - 6 1/8" | 0' - 1 9/16" | 0' - 0 7/8" | 0' - 0 11/16" | 0' - 0 7/16" |
| WT6X32.5 | 9.54 in² | 32.5 | 1' - 0" | 0' - 6 1/16" | 0' - 1 1/2" | 0' - 0 7/8" | 0' - 0 5/8" | 0' - 0 3/8" |
| WT6X29 | 8.52 in² | 29 | 0' - 10" | 0' - 6 1/8" | 0' - 1 1/2" | 0' - 0 7/8" | 0' - 0 5/8" | 0' - 0 3/8" |
| WT6X26.5 | 7.78 in² | 26.5 | 0' - 10" | 0' - 6" | 0' - 1 3/8" | 0' - 0 13/16" | 0' - 0 9/16" | 0' - 0 3/8" |
| WT6X25 | 7.3 in² | 25 | 0' - 8 1/16" | 0' - 6 1/8" | 0' - 1 1/2" | 0' - 0 7/8" | 0' - 0 5/8" | 0' - 0 3/8" |
| WT6X22.5 | 6.56 in² | 22.5 | 0' - 8 1/16" | 0' - 6" | 0' - 1 3/8" | 0' - 0 13/16" | 0' - 0 9/16" | 0' - 0 5/16" |
| WT6X20 | 5.84 in² | 20 | 0' - 8" | 0' - 6" | 0' - 1 3/8" | 0' - 0 7/8" | 0' - 0 1/2" | 0' - 0 5/16" |
| WT6X17.5 | 5.17 in² | 17.5 | 0' - 6 9/16" | 0' - 6 1/4" | 0' - 1 3/16" | 0' - 0 11/16" | 0' - 0 1/2" | 0' - 0 5/16" |
| WT6X15 | 4.4 in² | 15 | 0' - 6 1/2" | 0' - 6 3/16" | 0' - 1 1/8" | 0' - 0 11/16" | 0' - 0 7/16" | 0' - 0 1/4" |
| WT6X13 | 3.82 in² | 13 | 0' - 6 1/2" | 0' - 6 1/8" | 0' - 1 1/16" | 0' - 0 11/16" | 0' - 0 3/8" | 0' - 0 1/4" |
| WT6X11 | 3.24 in² | 11 | 0' - 4" | 0' - 6 3/16" | 0' - 0 15/16" | 0' - 0 1/2" | 0' - 0 7/16" | 0' - 0 1/4" |
| WT6X9.5 | 2.79 in² | 9.5 | 0' - 4" | 0' - 6 1/16" | 0' - 0 7/8" | 0' - 0 1/2" | 0' - 0 3/8" | 0' - 0 1/4" |
| WT6X8 | 2.36 in² | 8 | 0' - 4" | 0' - 6" | 0' - 0 13/16" | 0' - 0 9/16" | 0' - 0 1/4" | 0' - 0 1/4" |
| WT6X7 | 2.08 in² | 7 | 0' - 4" | 0' - 5 15/16" | 0' - 0 3/4" | 0' - 0 1/2" | 0' - 0 1/4" | 0' - 0 3/16" |
| WT5X56 | 16.5 in² | 56 | 0' - 10 3/8" | 0' - 5 11/16" | 0' - 1 15/16" | 0' - 0 11/16" | 0' - 1 1/4" | 0' - 0 3/4" |
| WT5X50 | 14.7 in² | 50 | 0' - 10 5/16" | 0' - 5 9/16" | 0' - 1 13/16" | 0' - 0 11/16" | 0' - 1 1/8" | 0' - 0 11/16" |
| WT5X44 | 12.9 in² | 44 | 0' - 10 5/16" | 0' - 5 7/16" | 0' - 1 11/16" | 0' - 0 11/16" | 0' - 1" | 0' - 0 5/8" |
| WT5X38.5 | 11.3 in² | 38.5 | 0' - 10 3/16" | 0' - 5 5/16" | 0' - 1 9/16" | 0' - 0 11/16" | 0' - 0 7/8" | 0' - 0 1/2" |
| WT5X34 | 10 in² | 34 | 0' - 10 1/8" | 0' - 5 3/16" | 0' - 1 7/16" | 0' - 0 11/16" | 0' - 0 3/4" | 0' - 0 1/2" |
| WT5X30 | 8.82 in² | 30 | 0' - 10 1/8" | 0' - 5 1/8" | 0' - 1 3/8" | 0' - 0 11/16" | 0' - 0 11/16" | 0' - 0 7/16" |
| WT5X27 | 7.91 in² | 27 | 0' - 10" | 0' - 5 1/16" | 0' - 1 5/16" | 0' - 0 11/16" | 0' - 0 5/8" | 0' - 0 3/8" |
| WT5X24.5 | 7.21 in² | 24.5 | 0' - 10" | 0' - 5" | 0' - 1 1/4" | 0' - 0 11/16" | 0' - 0 9/16" | 0' - 0 5/16" |
| WT5X22.5 | 6.63 in² | 22.5 | 0' - 8" | 0' - 5 1/16" | 0' - 1 5/16" | 0' - 0 11/16" | 0' - 0 5/8" | 0' - 0 3/8" |
| WT5X19.5 | 5.73 in² | 19.5 | 0' - 8" | 0' - 4 15/16" | 0' - 1 3/16" | 0' - 0 11/16" | 0' - 0 1/2" | 0' - 0 5/16" |
| WT5X16.5 | 4.85 in² | 16.5 | 0' - 7 15/16" | 0' - 4 7/8" | 0' - 1 1/8" | 0' - 0 11/16" | 0' - 0 7/16" | 0' - 0 5/16" |
| WT5X15 | 4.42 in² | 15 | 0' - 5 13/16" | 0' - 5 1/4" | 0' - 1 1/8" | 0' - 0 5/8" | 0' - 0 1/2" | 0' - 0 5/16" |
| WT5X13 | 3.81 in² | 13 | 0' - 5 3/4" | 0' - 5 3/16" | 0' - 1 1/16" | 0' - 0 5/8" | 0' - 0 7/16" | 0' - 0 1/4" |
| WT5X11 | 3.24 in² | 11 | 0' - 5 3/4" | 0' - 5 1/16" | 0' - 0 15/16" | 0' - 0 9/16" | 0' - 0 3/8" | 0' - 0 1/4" |
| WT5X9.5 | 2.81 in² | 9.5 | 0' - 4" | 0' - 5 1/8" | 0' - 0 15/16" | 0' - 0 9/16" | 0' - 0 3/8" | 0' - 0 1/4" |
| WT5X8.5 | 2.5 in² | 8.5 | 0' - 4" | 0' - 5 1/16" | 0' - 0 7/8" | 0' - 0 9/16" | 0' - 0 5/16" | 0' - 0 1/4" |
| WT5X7.5 | 2.21 in² | 7.5 | 0' - 4" | 0' - 5" | 0' - 0 13/16" | 0' - 0 9/16" | 0' - 0 1/4" | 0' - 0 1/4" |
| WT5X6 | 1.77 in² | 6 | 0' - 3 15/16" | 0' - 4 15/16" | 0' - 0 3/4" | 0' - 0 9/16" | 0' - 0 3/16" | 0' - 0 3/16" |
| WT4X33.5 | 9.84 in² | 33.5 | 0' - 8 1/4" | 0' - 4 1/2" | 0' - 1 5/8" | 0' - 0 11/16" | 0' - 0 15/16" | 0' - 0 9/16" |
| WT4X29 | 8.54 in² | 29 | 0' - 8 1/4" | 0' - 4 3/8" | 0' - 1 1/2" | 0' - 0 11/16" | 0' - 0 13/16" | 0' - 0 1/2" |
| WT4X24 | 7.05 in² | 24 | 0' - 8 1/8" | 0' - 4 1/4" | 0' - 1 3/8" | 0' - 0 11/16" | 0' - 0 11/16" | 0' - 0 3/8" |
| WT4X20 | 5.87 in² | 20 | 0' - 8 1/16" | 0' - 4 1/8" | 0' - 1 1/4" | 0' - 0 11/16" | 0' - 0 9/16" | 0' - 0 3/8" |
| WT4X17.5 | 5.14 in² | 17.5 | 0' - 8" | 0' - 4 1/16" | 0' - 1 3/16" | 0' - 0 11/16" | 0' - 0 1/2" | 0' - 0 5/16" |
| WT4X15.5 | 4.56 in² | 15.5 | 0' - 8" | 0' - 4" | 0' - 1 1/8" | 0' - 0 11/16" | 0' - 0 7/16" | 0' - 0 5/16" |
| WT4X14 | 4.12 in² | 14 | 0' - 6 9/16" | 0' - 4" | 0' - 0 15/16" | 0' - 0 1/2" | 0' - 0 7/16" | 0' - 0 5/16" |
| WT4X12 | 3.54 in² | 12 | 0' - 6 1/2" | 0' - 4" | 0' - 0 7/8" | 0' - 0 1/2" | 0' - 0 3/8" | 0' - 0 1/4" |
| WT4X10.5 | 3.08 in² | 10.5 | 0' - 5 1/4" | 0' - 4 1/8" | 0' - 0 7/8" | 0' - 0 1/2" | 0' - 0 3/8" | 0' - 0 1/4" |
| WT4X9 | 2.63 in² | 9 | 0' - 5 1/4" | 0' - 4 1/16" | 0' - 0 13/16" | 0' - 0 1/2" | 0' - 0 5/16" | 0' - 0 1/4" |
| WT4X7.5 | 2.22 in² | 7.5 | 0' - 4" | 0' - 4 1/16" | 0' - 0 13/16" | 0' - 0 1/2" | 0' - 0 5/16" | 0' - 0 1/4" |
| WT4X6.5 | 1.92 in² | 6.5 | 0' - 4" | 0' - 4" | 0' - 0 3/4" | 0' - 0 1/2" | 0' - 0 1/4" | 0' - 0 1/4" |
| WT4X5 | 1.48 in² | 5 | 0' - 3 15/16" | 0' - 3 15/16" | 0' - 0 11/16" | 0' - 0 1/2" | 0' - 0 3/16" | 0' - 0 3/16" |
| WT3X12.5 | 3.67 in² | 12.5 | 0' - 6 1/16" | 0' - 3 3/16" | 0' - 0 15/16" | 0' - 0 1/2" | 0' - 0 7/16" | 0' - 0 5/16" |
| WT3X10 | 2.94 in² | 10 | 0' - 6" | 0' - 3 1/8" | 0' - 0 7/8" | 0' - 0 1/2" | 0' - 0 3/8" | 0' - 0 1/4" |
| WT3X7.5 | 2.21 in² | 7.5 | 0' - 6" | 0' - 3" | 0' - 0 3/4" | 0' - 0 1/2" | 0' - 0 1/4" | 0' - 0 1/4" |
| WT3X8 | 2.37 in² | 8 | 0' - 4" | 0' - 3 1/8" | 0' - 0 7/8" | 0' - 0 1/2" | 0' - 0 3/8" | 0' - 0 1/4" |
| WT3X6 | 1.78 in² | 6 | 0' - 4" | 0' - 3" | 0' - 0 3/4" | 0' - 0 1/2" | 0' - 0 1/4" | 0' - 0 1/4" |
| WT3X4.5 | 1.34 in² | 4.5 | 0' - 3 15/16" | 0' - 2 15/16" | 0' - 0 11/16" | 0' - 0 1/2" | 0' - 0 3/16" | 0' - 0 3/16" |
| WT3X4.25 | 1.26 in² | 4.25 | 0' - 3 15/16" | 0' - 2 15/16" | 0' - 0 11/16" | 0' - 0 1/2" | 0' - 0 3/16" | 0' - 0 3/16" |
| WT2.5X9.5 | 2.78 in² | 9.5 | 0' - 5" | 0' - 2 9/16" | 0' - 0 13/16" | 0' - 0 3/8" | 0' - 0 7/16" | 0' - 0 1/4" |
| WT2.5X8 | 2.35 in² | 8 | 0' - 5" | 0' - 2 1/2" | 0' - 0 3/4" | 0' - 0 3/8" | 0' - 0 3/8" | 0' - 0 1/4" |
| WT2X6.5 | 1.91 in² | 6.5 | 0' - 4 1/16" | 0' - 2 1/16" | 0' - 0 3/4" | 0' - 0 3/8" | 0' - 0 3/8" | 0' - 0 1/4" |

## geometry (parser evidence)
native form markers: Sweep x1
no freeform markers — native parametric forms only
